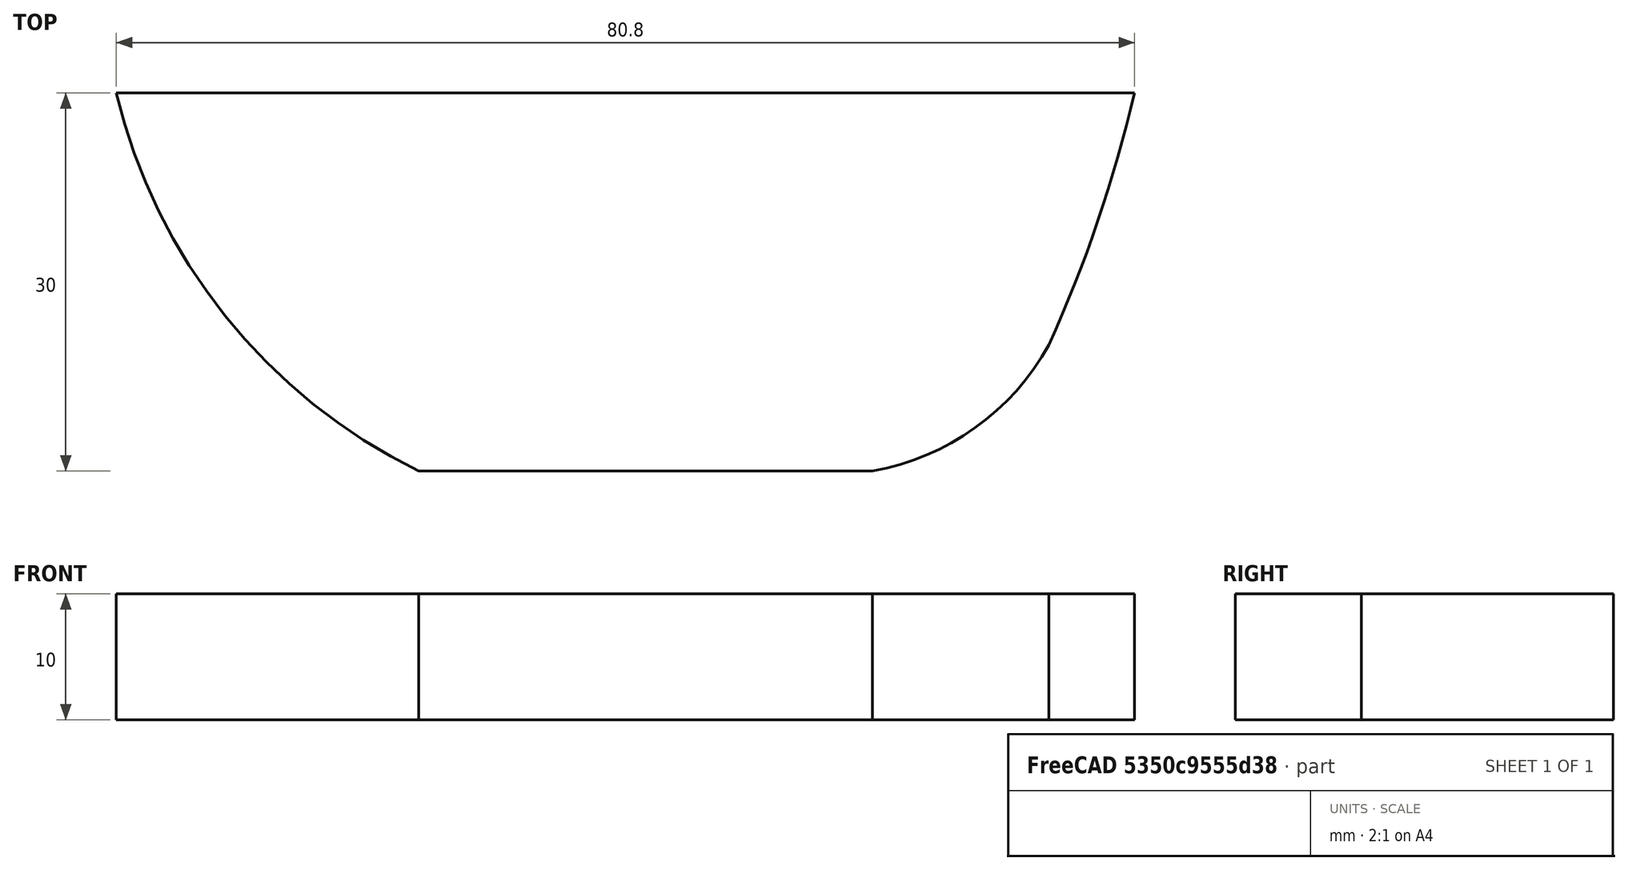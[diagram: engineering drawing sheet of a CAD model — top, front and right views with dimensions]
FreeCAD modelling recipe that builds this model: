
FCSTD DOCUMENT  (FreeCAD 0.15R4671 (Git))
Label: PalmFlange
License: All rights reserved
LicenseURL: http://en.wikipedia.org/wiki/All_rights_reserved
objects: Sketcher::SketchObject×1, PartDesign::Pad×1
note: 3 computed .brp shape members not serialized (recipe doc carries the construction recipe); baked Part::Feature solids carry a one-line shape summary decoded from their .brp

FEATURE [Sketcher::SketchObject] Sketch001
  sketch-geometry (7):
    g0: ArcOfCircle CenterX=20.5055 CenterY=13.6923 CenterZ=0 NormalX=0 NormalY=0 NormalZ=1 Radius=20 StartAngle=4.88802 EndAngle=5.77726
    g1: ArcOfCircle CenterX=-62.2638 CenterY=49.2457 CenterZ=0 NormalX=0 NormalY=0 NormalZ=1 Radius=110 StartAngle=5.85928 EndAngle=6.05161
    g2: ArcOfCircle CenterX=7.77666 CenterY=34.4213 CenterZ=0 NormalX=0 NormalY=0 NormalZ=1 Radius=45 StartAngle=3.3753 EndAngle=4.25737
    g3: GeomPoint [constr] X=0 Y=0 Z=0
    g4: LineSegment StartX=-12 StartY=-6 StartZ=0 EndX=24 EndY=-6 EndZ=0
    g5: LineSegment [constr] StartX=0 StartY=0 StartZ=0 EndX=0 EndY=-6 EndZ=0
    g6: LineSegment StartX=-36 StartY=24 StartZ=0 EndX=44.8 EndY=24 EndZ=0
  constraints (22):
    c: Coincident(g1,g0)
    c: Radius(g0) = 20
    c: Radius(g2) = 45
    c: Radius(g1) = 110
    c: DistanceY(g2,g3) = -24
    c: DistanceX(g2,g3) = 36
    c: DistanceX(g3,g0) = 38
    c: DistanceY(g3,g0) = 4
    c: Coincident(g-1,g3)
    c: Coincident(g4,g2)
    c: Coincident(g4,g0)
    c: Horizontal(g4)
    c: DistanceX(g4) = 36
    c: Coincident(g5,g-1)
    c: PointOnObject(g5,g4)
    c: Vertical(g5)
    c: DistanceX(g-1,g2) = -12
    c: DistanceY(g-1,g2) = -6
    c: Coincident(g6,g2)
    c: Horizontal(g6)
    c: Coincident(g6,g1)
    c: DistanceX(g-1,g1) = 44.8
FEATURE [PartDesign::Pad] Pad
  Length = 10
  Length2 = 100
  Sketch = -> Sketch001
  Type = 0
